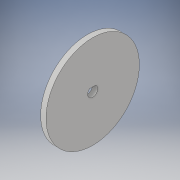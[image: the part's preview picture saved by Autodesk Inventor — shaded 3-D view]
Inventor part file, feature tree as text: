
AUTODESK INVENTOR PART (.ipt)
format: ipt  version: 2019 (Build 230136000, 136)  size: 101,888 bytes
history: native  units: in
note: dims shown in document units (in); Inventor stores cm internally (conversion verified against a paired STEP export)
features: extrude x2, sketch x2
ambient origin geometry x8: Origin, YZ Plane, XZ Plane, XY Plane, X Axis, Y Axis, Z Axis, Center Point
bodies: Solid1 (feature_tree)
feature tree (4):
  extrude  "Extrusion1"  Depth=0.125in TaperAngle=0.0deg
  extrude  "Extrusion2"  Depth=0.125in
  sketch  "Sketch1"  dims[d0=2.186in d1=0.125in d2=0.0in]
  sketch  "Sketch2"  dims[d3=0.2362in d4=0.2126in d5=0.125in d6=0.0in]
